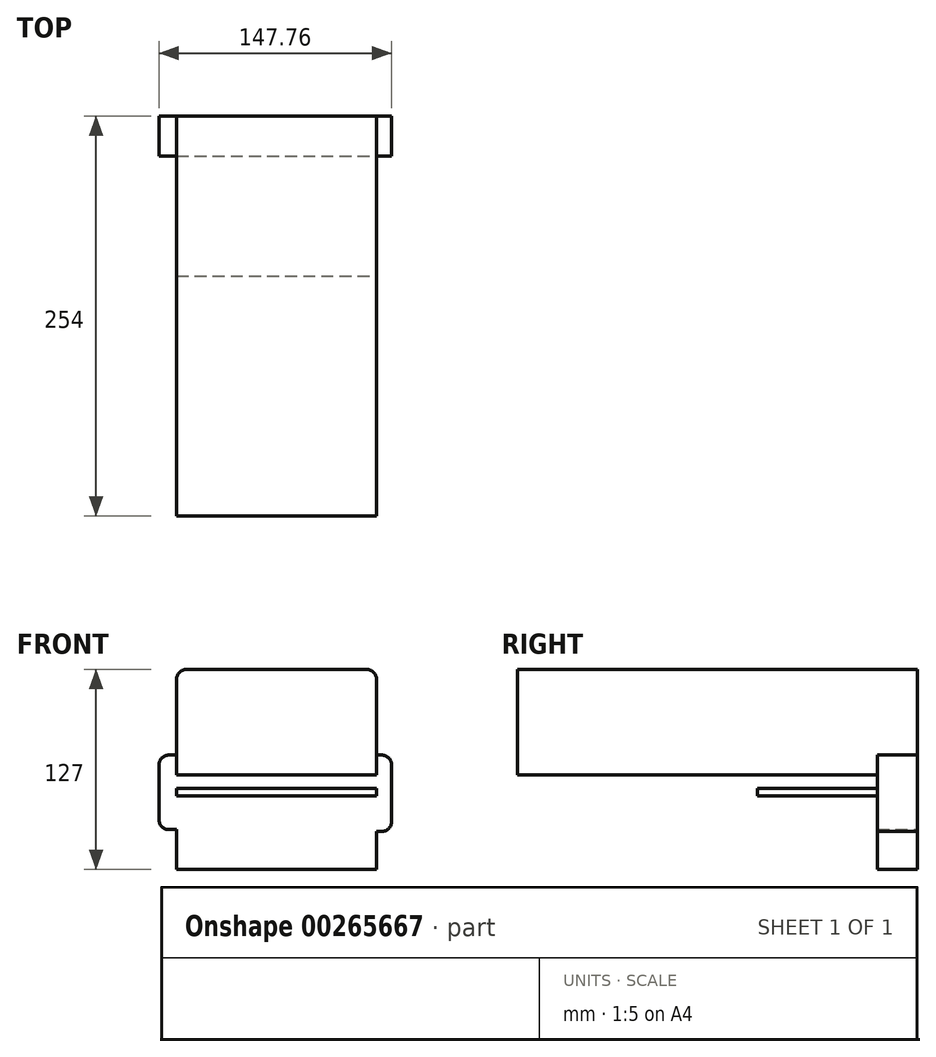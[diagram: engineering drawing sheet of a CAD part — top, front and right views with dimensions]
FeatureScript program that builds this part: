
annotation { "Feature Type Name" : "Feature", "Feature Type Description" : "" }
export const myFeature = defineFeature(function(context is Context, id is Id, definition is map)
    precondition{}
    {
        {
            var Q0;
            Q0=qCreatedBy(makeId("Front.planeOp"),FACE);
            var sketch = newSketch(context, id + "F0", { "sketchPlane" : qUnion([Q0])});
            skLineSegment(sketch, "E0", {"start": v(-56.55, 47.97) * mm, "end": v(-56.55, -72.68) * mm});
            skLineSegment(sketch, "E1", {"start": v(-50.2, 54.32) * mm, "end": v(64.1, 54.32) * mm});
            skLineSegment(sketch, "E2", {"start": v(70.45, 47.97) * mm, "end": v(70.45, -72.68) * mm});
            skLineSegment(sketch, "E3", {"start": v(-56.55, 38.13) * mm, "end": v(70.45, 38.13) * mm});
            skLineSegment(sketch, "E4", {"start": v(-56.55, -72.68) * mm, "end": v(70.45, -72.68) * mm});
            skLineSegment(sketch, "E5", {"start": v(6.95, -72.68) * mm, "end": v(6.95, -25.88) * mm});
            skLineSegment(sketch, "E6", {"start": v(-56.55, -25.88) * mm, "end": v(6.95, -25.88) * mm});
            skLineSegment(sketch, "E7", {"start": v(6.95, -25.88) * mm, "end": v(70.45, -25.88) * mm});
            skLineSegment(sketch, "E8", {"start": v(6.95, -25.88) * mm, "end": v(6.95, -21.1) * mm});
            skLineSegment(sketch, "E9", {"start": v(6.95, -21.1) * mm, "end": v(-56.55, -21.1) * mm});
            skLineSegment(sketch, "E10", {"start": v(6.95, -21.1) * mm, "end": v(70.45, -21.1) * mm});
            skLineSegment(sketch, "E11", {"start": v(70.45, 0) * mm, "end": v(73.66, 0) * mm});
            skLineSegment(sketch, "E12", {"start": v(70.45, -48.6) * mm, "end": v(73.66, -48.6) * mm});
            skLineSegment(sketch, "E13", {"start": v(80.01, -42.25) * mm, "end": v(80.01, -6.35) * mm});
            skPoint(sketch, "E14.visualSharp", {"position": v(80.01, -48.6) * mm});
            skArc(sketch, "E14.filletArc", {"start": v(73.66, -48.6) * mm, "mid": v(78.15, -46.74) * mm, "end": v(80.01, -42.25) * mm});
            skPoint(sketch, "E15.visualSharp", {"position": v(80.01, 0) * mm});
            skArc(sketch, "E15.filletArc", {"start": v(80.01, -6.35) * mm, "mid": v(78.15, -1.86) * mm, "end": v(73.66, 0) * mm});
            skPoint(sketch, "E16.startSnap0", {"position": v(-56.55, -9.18) * mm});
            skLineSegment(sketch, "E17", {"start": v(-56.55, -47.41) * mm, "end": v(-61.4, -47.41) * mm});
            skLineSegment(sketch, "E18", {"start": v(-56.55, 0) * mm, "end": v(-61.4, 0) * mm});
            skLineSegment(sketch, "E19", {"start": v(-67.75, -41.06) * mm, "end": v(-67.75, -6.35) * mm});
            skPoint(sketch, "E20.visualSharp", {"position": v(-67.75, -47.41) * mm});
            skArc(sketch, "E20.filletArc", {"start": v(-67.75, -41.06) * mm, "mid": v(-65.89, -45.55) * mm, "end": v(-61.4, -47.41) * mm});
            skPoint(sketch, "E21.visualSharp", {"position": v(-67.75, 0) * mm});
            skArc(sketch, "E21.filletArc", {"start": v(-61.4, 0) * mm, "mid": v(-65.89, -1.86) * mm, "end": v(-67.75, -6.35) * mm});
            skArc(sketch, "E22.filletArc", {"start": v(-50.2, 54.32) * mm, "mid": v(-54.7, 52.46) * mm, "end": v(-56.55, 47.97) * mm});
            skArc(sketch, "E23.filletArc", {"start": v(70.45, 47.97) * mm, "mid": v(68.59, 52.46) * mm, "end": v(64.1, 54.32) * mm});
            skSolve(sketch);
        }
        {
            var Q0;
            {var subQ0=sQuery(id+"F0.wireOp",EDGE,"E5");Q0=makeQuery(id+"F0.imprint","IMPRINT",FACE,{"disambiguationData":[TD([[makeQuery(id+"F0.imprint","IMPRINT",EDGE,{"derivedFrom":subQ0}),1.0]])]});}
            var Q1;
            {var subQ0=sQuery(id+"F0.wireOp",EDGE,"E5");Q1=makeQuery(id+"F0.imprint","IMPRINT",FACE,{"disambiguationData":[TD([[makeQuery(id+"F0.imprint","IMPRINT",EDGE,{"derivedFrom":subQ0}),-1.0]])]});}
            extrude(context, id + "F1", {"entities" : qUnion([Q0, Q1]), "depth" : 12.7 * mm});
        }
        {
            var Q0;
            {var subQ0=sQuery(id+"F0.wireOp",EDGE,"E6");Q0=makeQuery(id+"F0.imprint","IMPRINT",FACE,{"disambiguationData":[TD([[makeQuery(id+"F0.imprint","IMPRINT",EDGE,{"derivedFrom":subQ0}),1.0]])]});}
            var Q1;
            {var subQ0=sQuery(id+"F0.wireOp",EDGE,"E7");Q1=makeQuery(id+"F0.imprint","IMPRINT",FACE,{"disambiguationData":[TD([[makeQuery(id+"F0.imprint","IMPRINT",EDGE,{"derivedFrom":subQ0}),1.0]])]});}
            extrude(context, id + "F2", {"entities" : qUnion([Q0, Q1]), "operationType" : NewBodyOperationType.ADD, "depth" : 101.6 * mm});
        }
        {
            var Q0;
            {var subQ0=sQuery(id+"F0.wireOp",EDGE,"E1");Q0=makeQuery(id+"F0.imprint","IMPRINT",FACE,{"disambiguationData":[TD([[makeQuery(id+"F0.imprint","IMPRINT",EDGE,{"derivedFrom":subQ0}),-1.0]])]});}
            extrude(context, id + "F3", {"entities" : qUnion([Q0]), "depth" : 254 * mm});
        }
        {
            var Q0;
            {var subQ0=sQuery(id+"F0.wireOp",EDGE,"E11");Q0=makeQuery(id+"F0.imprint","IMPRINT",FACE,{"disambiguationData":[TD([[makeQuery(id+"F0.imprint","IMPRINT",EDGE,{"derivedFrom":subQ0}),-1.0]])]});}
            var Q1;
            {var subQ0=sQuery(id+"F0.wireOp",EDGE,"E17");Q1=makeQuery(id+"F0.imprint","IMPRINT",FACE,{"disambiguationData":[TD([[makeQuery(id+"F0.imprint","IMPRINT",EDGE,{"derivedFrom":subQ0}),-1.0]])]});}
            var Q2;
            Q2=makeQuery(id+"F1.opExtrude","CAP_FACE",FACE,{"disambiguationData":[OSD([sQuery(id+"F0.wireOp",EDGE,"E0"),sQuery(id+"F0.wireOp",EDGE,"E2"),sQuery(id+"F0.wireOp",EDGE,"E4"),sQuery(id+"F0.wireOp",EDGE,"E6"),sQuery(id+"F0.wireOp",EDGE,"E7")])],"isStart":false});
            extrude(context, id + "F4", {"entities" : qUnion([Q0, Q1, Q2]), "operationType" : NewBodyOperationType.ADD, "depth" : 2.54 * mm});
        }
        {
            var Q0;
            Q0=makeQuery(id+"F3.opExtrude","SWEPT_FACE",FACE,{"disambiguationData":[OSD([sQuery(id+"F0.wireOp",EDGE,"E3")])]});
            extrude(context, id + "F5", {"entities" : qUnion([Q0]), "operationType" : NewBodyOperationType.ADD, "depth" : 50.8 * mm});
        }
        {
            var Q0;
            Q0 = qSketchRegion(id + "F0", true);
            extrude(context, id + "F6", {"entities" : qUnion([Q0]), "operationType" : NewBodyOperationType.ADD, "depth" : 25.4 * mm});
        }
    });
